# Revit family: Specialty_Equipment-Covrit-Roofed_Enclosure-Single-rev2
name_source: partatom
category: Specialty Equipment
units: mm (PartAtom-declared; Revit-internal decimal feet)

## family parameters
Always vertical = Yes
Cut with Voids When Loaded = No
Enable Cutting in Views = No
Maintain Annotation Orientation = No
Part Type = Normal
Room Calculation Point = No
Round Connector Dimension = Use Diameter
Shared = No
Work Plane-Based = No

## types (5) — shared parameters
CD_# Panels Width = 2
CD_7' Wall = Yes
CD_8' Wall = No
CD_9' Wall = No
CD_Depth Max = 13' - 0"
CD_Depth Min = 11' - 0"
CD_Direct Bury = No
CD_Embeddment Offset = 0' - 0"
CD_Finish = Plastic-PVC-CityScapes-Vertical-Kona
CD_Finish Frame = Metal-Aluminum-Cityscapes-Electric_Black
CD_Height Roof Eave = 7' - 9"
CD_Height Roof Peak = 10' - 8"
CD_Height Wall = 7' - 0"
CD_Microsite = https://www.caddetails.com
CD_Product Documentation Link = https://cityscapesinc.com
CD_Product Name = Covrit Dumpster Enclosure
CD_Product Page = https://cityscapesinc.com
CD_Surface Mount = Yes
CD_Width Max = 22' - 0"
CD_Width Min = 11' - 0"
Default Elevation = 0' - 0"
Description = Dumpster Gates & Walls
Manufacturer = CityScapes
Type Comments = Surface Mounted Covrit System
URL = https://cityscapesinc.com

## per-type parameters (varying)
| type | CD_Depth | CD_Depth Requested | CD_Infill | CD_Post Spacing Depth | CD_Post Spacing Width | CD_Width | CD_Width Gate | CD_Width Requested | Model |
| 1111R | 11' - 0" | 11' - 0" | No | 5' - 6" | 5' - 6" | 11' - 0" | 5' - 6" | 11' - 0" | 1111R |
| 1111R (Infill) | 11' - 0" | 11' - 0" | Yes | 5' - 6" | 5' - 6" | 11' - 0" | 5' - 6" | 11' - 0" | 1111R |
| 1313R | 13' - 0" | 13' - 0" | No | 6' - 6" | 6' - 6" | 13' - 0" | 6' - 6" | 13' - 0" | 1111R |
| 1313R (Infill) | 13' - 0" | 13' - 0" | Yes | 6' - 6" | 6' - 6" | 13' - 0" | 6' - 6" | 13' - 0" | 1313R |
| Custom Size | 13' - 0" | 13' - 0" | No | 6' - 6" | 6' - 6" | 13' - 0" | 6' - 6" | 13' - 0" | Custom |

## geometry (parser evidence)
native form markers: Sweep x27
no freeform markers — native parametric forms only
